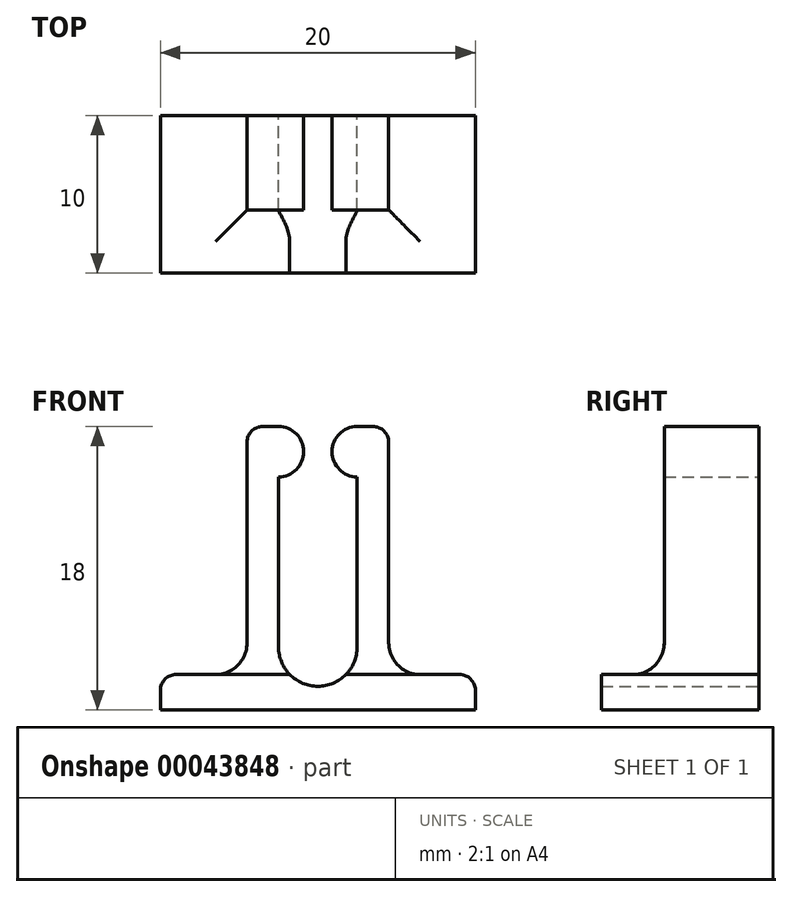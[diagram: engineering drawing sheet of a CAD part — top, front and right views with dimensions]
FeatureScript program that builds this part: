
annotation { "Feature Type Name" : "Feature", "Feature Type Description" : "" }
export const myFeature = defineFeature(function(context is Context, id is Id, definition is map)
    precondition{}
    {
        {
            var Q0;
            Q0=qCreatedBy(makeId("Front.planeOp"),FACE);
            var sketch = newSketch(context, id + "F0", { "sketchPlane" : qUnion([Q0])});
            skLineSegment(sketch, "E0", {"start": v(0, 0) * mm, "end": v(0, 10) * mm, "construction": true});
            skLineSegment(sketch, "E1", {"start": v(0, 0) * mm, "end": v(10, 0) * mm});
            skLineSegment(sketch, "E2", {"start": v(10, 0) * mm, "end": v(10, 2.25) * mm});
            skLineSegment(sketch, "E3", {"start": v(10, 2.25) * mm, "end": v(6.5, 2.25) * mm});
            skLineSegment(sketch, "E4", {"start": v(4.5, 4.25) * mm, "end": v(4.5, 18) * mm});
            skLineSegment(sketch, "E5", {"start": v(4.5, 18) * mm, "end": v(2.5, 18) * mm});
            skLineSegment(sketch, "E6.MirrorCS", {"start": v(-10, 0) * mm, "end": v(-10, 2.25) * mm});
            skLineSegment(sketch, "E7.MirrorCS", {"start": v(-4.5, 18) * mm, "end": v(-2.5, 18) * mm});
            skLineSegment(sketch, "E8.MirrorCS", {"start": v(-2.5, 14.8) * mm, "end": v(-2.5, 4) * mm});
            skLineSegment(sketch, "E9.MirrorCS", {"start": v(-10, 2.25) * mm, "end": v(-6.5, 2.25) * mm});
            skLineSegment(sketch, "E10.MirrorCS", {"start": v(0, 0) * mm, "end": v(-10, 0) * mm});
            skLineSegment(sketch, "E11.MirrorCS", {"start": v(-4.5, 4.25) * mm, "end": v(-4.5, 18) * mm});
            skLineSegment(sketch, "E12", {"start": v(-2.5, 4) * mm, "end": v(2.5, 4) * mm, "construction": true});
            skArc(sketch, "E13", {"start": v(-2.5, 4) * mm, "mid": v(0, 1.5) * mm, "end": v(2.5, 4) * mm});
            skArc(sketch, "E14", {"start": v(-2.5, 14.8) * mm, "mid": v(-0.9, 16.4) * mm, "end": v(-2.5, 18) * mm});
            skArc(sketch, "E15", {"start": v(2.5, 18) * mm, "mid": v(0.9, 16.4) * mm, "end": v(2.5, 14.8) * mm});
            skLineSegment(sketch, "E16.trimOffspring", {"start": v(2.5, 14.8) * mm, "end": v(2.5, 4) * mm});
            skLineSegment(sketch, "E17", {"start": v(-2.5, 14.8) * mm, "end": v(2.5, 14.8) * mm, "construction": true});
            skPoint(sketch, "E18.visualSharp", {"position": v(-4.5, 2.25) * mm});
            skArc(sketch, "E18.filletArc", {"start": v(-6.5, 2.25) * mm, "mid": v(-5.09, 2.84) * mm, "end": v(-4.5, 4.25) * mm});
            skPoint(sketch, "E19.visualSharp", {"position": v(4.5, 2.25) * mm});
            skArc(sketch, "E19.filletArc", {"start": v(4.5, 4.25) * mm, "mid": v(5.09, 2.84) * mm, "end": v(6.5, 2.25) * mm});
            skSolve(sketch);
        }
        {
            var Q0;
            Q0 = qSketchRegion(id + "F0", true);
            extrude(context, id + "F1", {"entities" : qUnion([Q0]), "depth" : 10 * mm});
        }
        {
            var Q0;
            Q0=makeQuery(id+"F1.opExtrude","SWEPT_EDGE",EDGE,{"disambiguationData":[OSD([sQuery(id+"F0.wireOp",EDGE,"E4"),sQuery(id+"F0.wireOp",EDGE,"E5")])]});
            fillet(context, id + "F2", {"entities" : qUnion([Q0]), "radius" : 1 * mm, "tangentPropagation" : true, "allowEdgeOverflow" : false});
        }
        {
            var Q0;
            Q0=makeQuery(id+"F1.opExtrude","SWEPT_EDGE",EDGE,{"disambiguationData":[OSD([sQuery(id+"F0.wireOp",EDGE,"E7.MirrorCS"),sQuery(id+"F0.wireOp",EDGE,"E11.MirrorCS")])]});
            fillet(context, id + "F3", {"entities" : qUnion([Q0]), "radius" : 1 * mm, "tangentPropagation" : true, "allowEdgeOverflow" : false});
        }
        {
            var Q0;
            Q0=makeQuery(id+"F1.opExtrude","SWEPT_EDGE",EDGE,{"disambiguationData":[OSD([sQuery(id+"F0.wireOp",EDGE,"E2"),sQuery(id+"F0.wireOp",EDGE,"E3")])]});
            fillet(context, id + "F4", {"entities" : qUnion([Q0]), "radius" : 1 * mm, "tangentPropagation" : true, "allowEdgeOverflow" : false});
        }
        {
            var Q0;
            Q0=makeQuery(id+"F1.opExtrude","SWEPT_EDGE",EDGE,{"disambiguationData":[OSD([sQuery(id+"F0.wireOp",EDGE,"E6.MirrorCS"),sQuery(id+"F0.wireOp",EDGE,"E9.MirrorCS")])]});
            fillet(context, id + "F5", {"entities" : qUnion([Q0]), "radius" : 1 * mm, "tangentPropagation" : true, "allowEdgeOverflow" : false});
        }
        {
            var Q0;
            Q0=qCreatedBy(makeId("Right.planeOp"),FACE);
            var sketch = newSketch(context, id + "F6", { "sketchPlane" : qUnion([Q0])});
            skLineSegment(sketch, "E20.0", {"start": v(-10, 18) * mm, "end": v(-6, 18) * mm});
            skLineSegment(sketch, "E21", {"start": v(-6, 18) * mm, "end": v(-6, 2.25) * mm});
            skLineSegment(sketch, "E22.0", {"start": v(-10, 2.25) * mm, "end": v(-6, 2.25) * mm});
            skPoint(sketch, "E23.orphan", {"position": v(0, 2.25) * mm});
            skPoint(sketch, "E24.orphan", {"position": v(0, 18) * mm});
            skLineSegment(sketch, "E25", {"start": v(-10, 2.25) * mm, "end": v(-10, 18) * mm});
            skSolve(sketch);
        }
        {
            var Q0;
            Q0 = qSketchRegion(id + "F6", true);
            extrude(context, id + "F7", {"entities" : qUnion([Q0]), "operationType" : NewBodyOperationType.REMOVE, "endBound" : BoundingType.THROUGH_ALL, "oppositeDirection" : true, "depth" : 25.4 * mm, "hasSecondDirection" : true, "secondDirectionBound" : SecondDirectionBoundingType.THROUGH_ALL, "secondDirectionOppositeDirection" : false, "secondDirectionDepth" : 25.4 * mm});
        }
        {
            var Q0;
            Q0=makeQuery(id+"F7.boolean.opBoolean","COPY",EDGE,{"disambiguationData":[OD(1.0)],"derivedFrom":makeQuery(id+"F7.opExtrude","SWEPT_EDGE",EDGE,{"disambiguationData":[OSD([sQuery(id+"F6.wireOp",EDGE,"E21"),sQuery(id+"F6.wireOp",EDGE,"E22.0")])]})});
            var Q1;
            Q1=makeQuery(id+"F7.boolean.opBoolean","COPY",EDGE,{"disambiguationData":[OD(0.0)],"derivedFrom":makeQuery(id+"F7.opExtrude","SWEPT_EDGE",EDGE,{"disambiguationData":[OSD([sQuery(id+"F6.wireOp",EDGE,"E21"),sQuery(id+"F6.wireOp",EDGE,"E22.0")])]})});
            fillet(context, id + "F8", {"entities" : qUnion([Q0, Q1]), "radius" : 2 * mm, "tangentPropagation" : true, "allowEdgeOverflow" : false});
        }
    });
